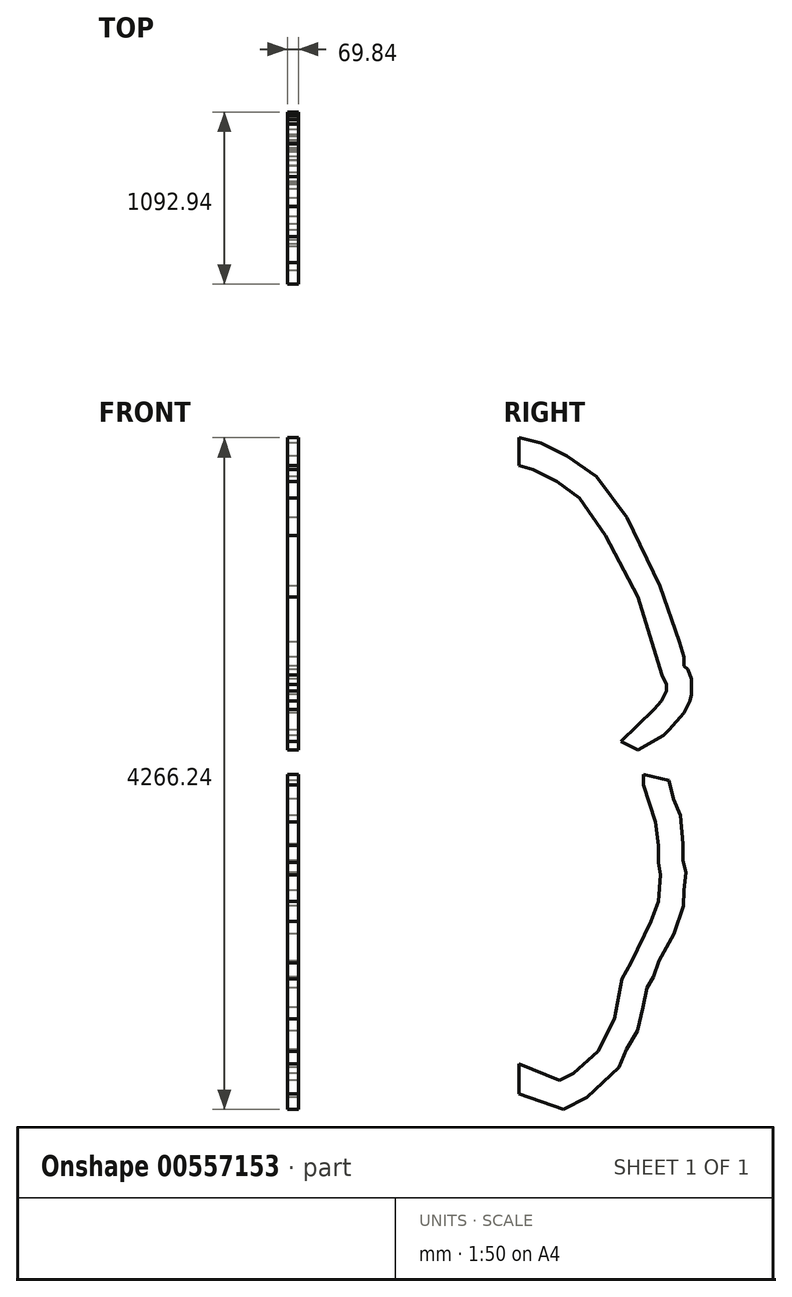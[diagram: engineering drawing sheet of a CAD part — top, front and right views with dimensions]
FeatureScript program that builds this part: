
annotation { "Feature Type Name" : "Feature", "Feature Type Description" : "" }
export const myFeature = defineFeature(function(context is Context, id is Id, definition is map)
    precondition{}
    {
        {
            var Q0;
            Q0=qCreatedBy(makeId("Right.planeOp"),FACE);
            var sketch = newSketch(context, id + "F0", { "sketchPlane" : qUnion([Q0])});
            skLineSegment(sketch, "E0", {"start": v(0, 98.94) * mm, "end": v(0, 288.44) * mm});
            skLineSegment(sketch, "E1", {"start": v(0, 288.44) * mm, "end": v(254.98, 183.9) * mm});
            skLineSegment(sketch, "E2", {"start": v(254.98, 183.9) * mm, "end": v(344.48, 228.7) * mm});
            skLineSegment(sketch, "E3", {"start": v(344.48, 228.7) * mm, "end": v(500.55, 369.72) * mm});
            skLineSegment(sketch, "E4", {"start": v(500.55, 369.72) * mm, "end": v(605.85, 574.67) * mm});
            skLineSegment(sketch, "E5", {"start": v(605.85, 574.67) * mm, "end": v(652.85, 830.4) * mm});
            skLineSegment(sketch, "E6", {"start": v(652.85, 830.4) * mm, "end": v(709.06, 930.13) * mm});
            skLineSegment(sketch, "E7", {"start": v(709.06, 930.13) * mm, "end": v(837.93, 1192.67) * mm});
            skLineSegment(sketch, "E8", {"start": v(837.93, 1192.67) * mm, "end": v(883.55, 1321.1) * mm});
            skLineSegment(sketch, "E9", {"start": v(883.55, 1321.1) * mm, "end": v(898.3, 1488.58) * mm});
            skLineSegment(sketch, "E10", {"start": v(898.3, 1488.58) * mm, "end": v(883.55, 1569.33) * mm});
            skLineSegment(sketch, "E11", {"start": v(883.55, 1569.33) * mm, "end": v(883.55, 1675.42) * mm});
            skLineSegment(sketch, "E12", {"start": v(883.55, 1675.42) * mm, "end": v(865.04, 1825.84) * mm});
            skLineSegment(sketch, "E13", {"start": v(865.04, 1825.84) * mm, "end": v(789.04, 2060.2) * mm});
            skLineSegment(sketch, "E14", {"start": v(789.04, 2060.2) * mm, "end": v(789.04, 2126.7) * mm});
            skLineSegment(sketch, "E15", {"start": v(789.04, 2126.7) * mm, "end": v(950.55, 2090.28) * mm});
            skLineSegment(sketch, "E16", {"start": v(950.55, 2090.28) * mm, "end": v(980.63, 1971.52) * mm});
            skLineSegment(sketch, "E17", {"start": v(980.63, 1971.52) * mm, "end": v(1023.38, 1868.6) * mm});
            skLineSegment(sketch, "E18", {"start": v(1023.38, 1868.6) * mm, "end": v(1040.8, 1686.5) * mm});
            skLineSegment(sketch, "E19", {"start": v(1040.8, 1686.5) * mm, "end": v(1040.8, 1580.41) * mm});
            skLineSegment(sketch, "E20", {"start": v(1040.8, 1580.41) * mm, "end": v(1059.8, 1506) * mm});
            skLineSegment(sketch, "E21", {"start": v(1059.8, 1506) * mm, "end": v(1046.14, 1390.8) * mm});
            skLineSegment(sketch, "E22", {"start": v(1046.14, 1390.8) * mm, "end": v(1041.82, 1293.32) * mm});
            skLineSegment(sketch, "E23", {"start": v(1041.82, 1293.32) * mm, "end": v(981.33, 1114.07) * mm});
            skLineSegment(sketch, "E24", {"start": v(981.33, 1114.07) * mm, "end": v(888, 942.97) * mm});
            skLineSegment(sketch, "E25", {"start": v(888, 942.97) * mm, "end": v(851.24, 842.57) * mm});
            skLineSegment(sketch, "E26", {"start": v(851.24, 842.57) * mm, "end": v(810.23, 773.28) * mm});
            skLineSegment(sketch, "E27", {"start": v(810.23, 773.28) * mm, "end": v(786.2, 648.84) * mm});
            skLineSegment(sketch, "E28", {"start": v(786.2, 648.84) * mm, "end": v(750.84, 497.54) * mm});
            skLineSegment(sketch, "E29", {"start": v(750.84, 497.54) * mm, "end": v(681.55, 381.58) * mm});
            skLineSegment(sketch, "E30", {"start": v(681.55, 381.58) * mm, "end": v(633.47, 265.63) * mm});
            skLineSegment(sketch, "E31", {"start": v(633.47, 265.63) * mm, "end": v(430.02, 77.32) * mm});
            skLineSegment(sketch, "E32", {"start": v(430.02, 77.32) * mm, "end": v(280.06, 0) * mm});
            skLineSegment(sketch, "E33", {"start": v(280.06, 0) * mm, "end": v(0, 98.94) * mm});
            skLineSegment(sketch, "E34", {"start": v(752.42, 2281.87) * mm, "end": v(644.44, 2335.86) * mm});
            skLineSegment(sketch, "E35", {"start": v(644.44, 2335.86) * mm, "end": v(854.41, 2539.84) * mm});
            skLineSegment(sketch, "E36", {"start": v(854.41, 2539.84) * mm, "end": v(904.4, 2593.84) * mm});
            skLineSegment(sketch, "E37", {"start": v(904.4, 2593.84) * mm, "end": v(936.4, 2657.83) * mm});
            skLineSegment(sketch, "E38", {"start": v(936.4, 2657.83) * mm, "end": v(936.4, 2700.3) * mm});
            skLineSegment(sketch, "E39", {"start": v(936.4, 2700.3) * mm, "end": v(905.59, 2758.64) * mm});
            skLineSegment(sketch, "E40", {"start": v(905.59, 2758.64) * mm, "end": v(754.78, 3255.93) * mm});
            skLineSegment(sketch, "E41", {"start": v(754.78, 3255.93) * mm, "end": v(548.54, 3646.34) * mm});
            skLineSegment(sketch, "E42", {"start": v(548.54, 3646.34) * mm, "end": v(383.54, 3884.37) * mm});
            skLineSegment(sketch, "E43", {"start": v(383.54, 3884.37) * mm, "end": v(238.81, 3988.47) * mm});
            skLineSegment(sketch, "E44", {"start": v(238.81, 3988.47) * mm, "end": v(86.47, 4064.64) * mm});
            skLineSegment(sketch, "E45", {"start": v(86.47, 4064.64) * mm, "end": v(0, 4090.92) * mm});
            skLineSegment(sketch, "E46", {"start": v(0, 4090.92) * mm, "end": v(0, 4266.24) * mm});
            skLineSegment(sketch, "E47", {"start": v(0, 4266.24) * mm, "end": v(138.3, 4233.22) * mm});
            skLineSegment(sketch, "E48", {"start": v(138.3, 4233.22) * mm, "end": v(219.2, 4192.78) * mm});
            skLineSegment(sketch, "E49", {"start": v(219.2, 4192.78) * mm, "end": v(302.3, 4151.23) * mm});
            skLineSegment(sketch, "E50", {"start": v(302.3, 4151.23) * mm, "end": v(491.88, 4021.35) * mm});
            skLineSegment(sketch, "E51", {"start": v(491.88, 4021.35) * mm, "end": v(683.12, 3759.95) * mm});
            skLineSegment(sketch, "E52", {"start": v(683.12, 3759.95) * mm, "end": v(893.64, 3325.73) * mm});
            skLineSegment(sketch, "E53", {"start": v(893.64, 3325.73) * mm, "end": v(1017.6, 2967.62) * mm});
            skLineSegment(sketch, "E54", {"start": v(1017.6, 2967.62) * mm, "end": v(1046.33, 2872.57) * mm});
            skLineSegment(sketch, "E55", {"start": v(1046.33, 2872.57) * mm, "end": v(1046.33, 2815.1) * mm});
            skLineSegment(sketch, "E56", {"start": v(1046.33, 2815.1) * mm, "end": v(1069.9, 2793.82) * mm});
            skLineSegment(sketch, "E57", {"start": v(1069.9, 2793.82) * mm, "end": v(1092.94, 2733.35) * mm});
            skLineSegment(sketch, "E58", {"start": v(1092.94, 2733.35) * mm, "end": v(1092.94, 2634.49) * mm});
            skLineSegment(sketch, "E59", {"start": v(1092.94, 2634.49) * mm, "end": v(1085.53, 2593.84) * mm});
            skLineSegment(sketch, "E60", {"start": v(1085.53, 2593.84) * mm, "end": v(1047.4, 2517.58) * mm});
            skLineSegment(sketch, "E61", {"start": v(1047.4, 2517.58) * mm, "end": v(950.55, 2409.08) * mm});
            skLineSegment(sketch, "E62", {"start": v(950.55, 2409.08) * mm, "end": v(916.19, 2373.81) * mm});
            skLineSegment(sketch, "E63", {"start": v(916.19, 2373.81) * mm, "end": v(752.42, 2281.87) * mm});
            skSolve(sketch);
        }
        {
            var Q0;
            Q0 = qSketchRegion(id + "F0", true);
            extrude(context, id + "F1", {"entities" : qUnion([Q0]), "depth" : 69.85 * mm, "offsetDistance" : 25.4 * mm, "symmetric" : true});
        }
    });
